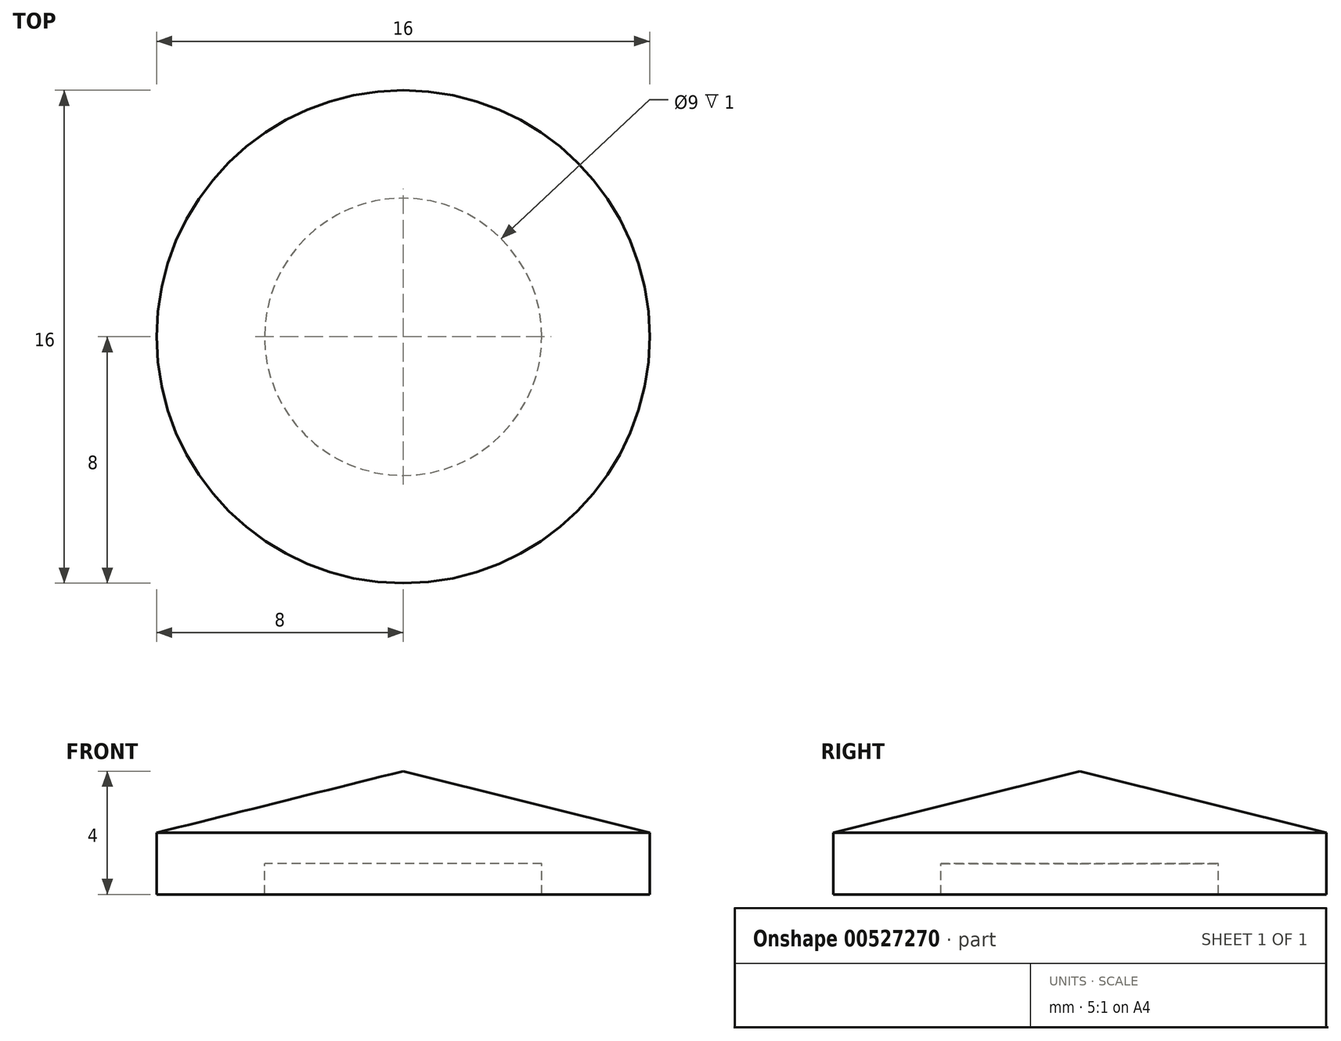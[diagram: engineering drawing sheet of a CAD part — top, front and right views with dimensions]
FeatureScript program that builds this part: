
annotation { "Feature Type Name" : "Feature", "Feature Type Description" : "" }
export const myFeature = defineFeature(function(context is Context, id is Id, definition is map)
    precondition{}
    {
        {
            var Q0;
            Q0=qCreatedBy(makeId("Top.planeOp"),FACE);
            var sketch = newSketch(context, id + "F0", { "sketchPlane" : qUnion([Q0])});
            skCircle(sketch, "E0", {"center": v(0, 0) * mm, "radius": 8 * mm});
            skCircle(sketch, "E1", {"center": v(0, 0) * mm, "radius": 4.5 * mm});
            skSolve(sketch);
        }
        {
            var Q0;
            Q0=qCreatedBy(makeId("Front.planeOp"),FACE);
            var sketch = newSketch(context, id + "F1", { "sketchPlane" : qUnion([Q0])});
            skLineSegment(sketch, "E2", {"start": v(0, 0) * mm, "end": v(0, 2) * mm});
            skLineSegment(sketch, "E3", {"start": v(0, 0) * mm, "end": v(8, 0) * mm});
            skLineSegment(sketch, "E4", {"start": v(8, 0) * mm, "end": v(0, 2) * mm});
            skSolve(sketch);
        }
        {
            var Q0;
            Q0=makeQuery(id+"F0.imprint","IMPRINT",FACE,{"disambiguationData":[TD([[makeQuery(id+"F0.imprint","IMPRINT",EDGE,{"derivedFrom":sQuery(id+"F0.wireOp",EDGE,"E0")}),1.0]])]});
            extrude(context, id + "F2", {"entities" : qUnion([Q0]), "oppositeDirection" : true, "depth" : 2 * mm, "offsetDistance" : 25 * mm});
        }
        {
            var Q0;
            Q0=makeQuery(id+"F0.imprint","IMPRINT",FACE,{"disambiguationData":[TD([[makeQuery(id+"F0.imprint","IMPRINT",EDGE,{"derivedFrom":sQuery(id+"F0.wireOp",EDGE,"E1")}),1.0]])]});
            extrude(context, id + "F3", {"entities" : qUnion([Q0]), "operationType" : NewBodyOperationType.ADD, "oppositeDirection" : true, "depth" : 1 * mm, "offsetDistance" : 25 * mm});
        }
        {
            var Q0;
            Q0=makeQuery(id+"F1.imprint","IMPRINT",FACE,{"disambiguationData":[TD([[makeQuery(id+"F1.imprint","IMPRINT",EDGE,{"derivedFrom":sQuery(id+"F1.wireOp",EDGE,"E2")}),-1.0]])]});
            var Q1;
            Q1=sQuery(id+"F1.wireOp",EDGE,"E2");
            revolve(context, id + "F4", {"operationType" : NewBodyOperationType.ADD, "entities" : qUnion([Q0]), "axis" : qUnion([Q1]), "revolveType" : RevolveType.FULL});
        }
    });
